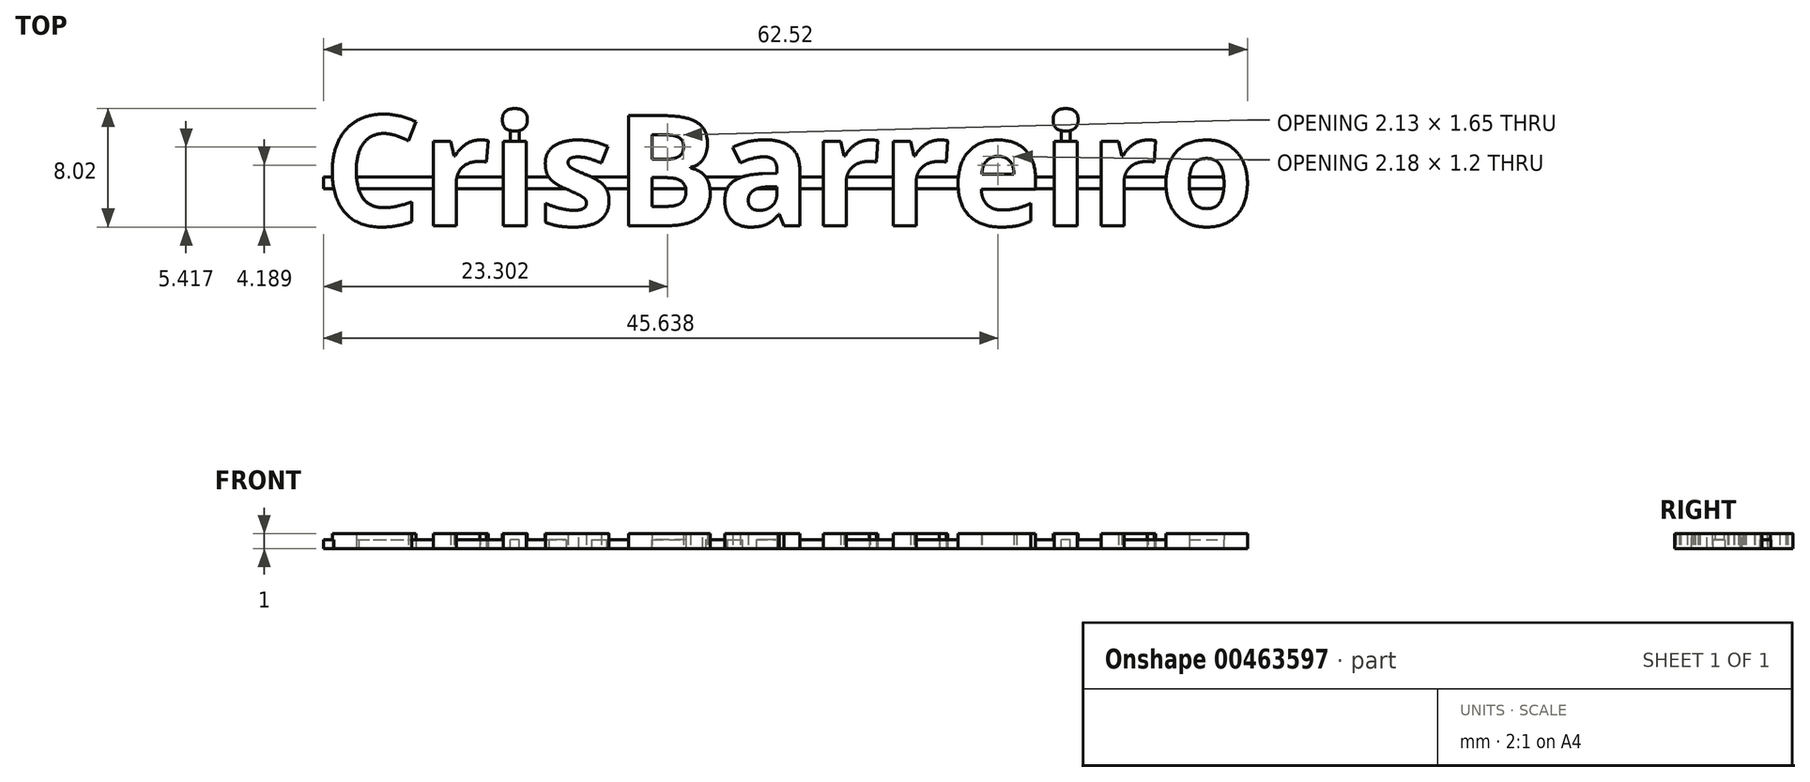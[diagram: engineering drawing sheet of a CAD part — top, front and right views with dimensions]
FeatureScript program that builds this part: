
annotation { "Feature Type Name" : "Feature", "Feature Type Description" : "" }
export const myFeature = defineFeature(function(context is Context, id is Id, definition is map)
    precondition{}
    {
        {
            var Q0;
            Q0=qCreatedBy(makeId("Top.planeOp"),FACE);
            var sketch = newSketch(context, id + "F0", { "sketchPlane" : qUnion([Q0])});
            skText(sketch, "E0", { "text": "CrisBarreiro", "fontName": "OpenSans-Bold.ttf"});
            const initialGuessF0  = {"E0": [0, -0.0075, 1, 0, 0.0075]};
            skSetInitialGuess(sketch, initialGuessF0);
            skSolve(sketch);
        }
        {
            var Q0;
            Q0 = qSketchRegion(id + "F0", true);
            extrude(context, id + "F1", {"entities" : qUnion([Q0]), "depth" : 1 * mm});
        }
        {
            var Q0;
            Q0=qCreatedBy(makeId("Top.planeOp"),FACE);
            var sketch = newSketch(context, id + "F2", { "sketchPlane" : qUnion([Q0])});
            skLineSegment(sketch, "E1.bottom", {"start": v(0, -4.2) * mm, "end": v(61.96, -4.2) * mm});
            skLineSegment(sketch, "E1.top", {"start": v(0, -5.02) * mm, "end": v(61.96, -5.02) * mm});
            skLineSegment(sketch, "E1.left", {"start": v(0, -4.2) * mm, "end": v(0, -5.02) * mm});
            skLineSegment(sketch, "E1.right", {"start": v(61.96, -4.2) * mm, "end": v(61.96, -5.02) * mm});
            skSolve(sketch);
        }
        {
            var Q0;
            Q0 = qSketchRegion(id + "F2", true);
            extrude(context, id + "F3", {"entities" : qUnion([Q0]), "operationType" : NewBodyOperationType.ADD, "depth" : 0.6 * mm});
        }
        {
            var Q0;
            Q0=makeQuery(id+"F1.opExtrude","CAP_FACE",FACE,{"disambiguationData":[OSD([sQuery(id+"F0.wireOp",EDGE,"E0.sketch_text.stroke-28"),sQuery(id+"F0.wireOp",EDGE,"E0.sketch_text.stroke-29"),sQuery(id+"F0.wireOp",EDGE,"E0.sketch_text.stroke-30"),sQuery(id+"F0.wireOp",EDGE,"E0.sketch_text.stroke-31"),sQuery(id+"F0.wireOp",EDGE,"E0.sketch_text.stroke-32")])],"isStart":true});
            var sketch = newSketch(context, id + "F4", { "sketchPlane" : qUnion([Q0])});
            skLineSegment(sketch, "E2", {"start": v(12.96, 0.32) * mm, "end": v(12.96, 2.99) * mm});
            skLineSegment(sketch, "E3", {"start": v(12.96, 2.99) * mm, "end": v(12.66, 2.99) * mm});
            skLineSegment(sketch, "E4.bottom", {"start": v(12.66, 2.99) * mm, "end": v(13.26, 2.99) * mm});
            skLineSegment(sketch, "E4.top", {"start": v(12.66, 0.32) * mm, "end": v(13.26, 0.32) * mm});
            skLineSegment(sketch, "E4.left", {"start": v(12.66, 2.99) * mm, "end": v(12.66, 0.32) * mm});
            skLineSegment(sketch, "E4.right", {"start": v(13.26, 2.99) * mm, "end": v(13.26, 0.32) * mm});
            skSolve(sketch);
        }
        {
            var Q0;
            Q0 = qSketchRegion(id + "F4", true);
            extrude(context, id + "F5", {"entities" : qUnion([Q0]), "operationType" : NewBodyOperationType.ADD, "oppositeDirection" : true, "depth" : 0.6 * mm});
        }
        {
            var Q0;
            Q0=makeQuery(id+"F1.opExtrude","CAP_FACE",FACE,{"disambiguationData":[OSD([sQuery(id+"F0.wireOp",EDGE,"E0.sketch_text.stroke-159"),sQuery(id+"F0.wireOp",EDGE,"E0.sketch_text.stroke-160"),sQuery(id+"F0.wireOp",EDGE,"E0.sketch_text.stroke-161"),sQuery(id+"F0.wireOp",EDGE,"E0.sketch_text.stroke-162"),sQuery(id+"F0.wireOp",EDGE,"E0.sketch_text.stroke-163")])],"isStart":true});
            var sketch = newSketch(context, id + "F6", { "sketchPlane" : qUnion([Q0])});
            skLineSegment(sketch, "E5", {"start": v(50.23, 0.25) * mm, "end": v(50.23, 2.62) * mm});
            skLineSegment(sketch, "E6", {"start": v(50.23, 2.62) * mm, "end": v(49.93, 2.62) * mm});
            skLineSegment(sketch, "E7.bottom", {"start": v(49.93, 2.62) * mm, "end": v(50.53, 2.62) * mm});
            skLineSegment(sketch, "E7.top", {"start": v(49.93, 0.26) * mm, "end": v(50.53, 0.26) * mm});
            skLineSegment(sketch, "E7.left", {"start": v(49.93, 2.62) * mm, "end": v(49.93, 0.26) * mm});
            skLineSegment(sketch, "E7.right", {"start": v(50.53, 2.62) * mm, "end": v(50.53, 0.26) * mm});
            skSolve(sketch);
        }
        {
            var Q0;
            Q0 = qSketchRegion(id + "F6", true);
            extrude(context, id + "F7", {"entities" : qUnion([Q0]), "operationType" : NewBodyOperationType.ADD, "oppositeDirection" : true, "depth" : 0.6 * mm});
        }
    });
